FCSTD DOCUMENT  (FreeCAD 0.19R24276 (Git))
Label: Temp_place_bear
License: All rights reserved
LicenseURL: http://en.wikipedia.org/wiki/All_rights_reserved
objects: Sketcher::SketchObject×1, PartDesign::Body×1
note: 2 computed .brp shape members not serialized (recipe doc carries the construction recipe); baked Part::Feature solids carry a one-line shape summary decoded from their .brp

FEATURE [Sketcher::SketchObject] Sketch
  FullyConstrained = false
  MapMode = 5
  Support = -> [XY_Plane]
  sketch-geometry (24):
    g0: LineSegment StartX=0 StartY=0 StartZ=0 EndX=34.4274 EndY=0 EndZ=0
    g1: LineSegment StartX=34.4274 StartY=0 StartZ=0 EndX=34.4274 EndY=10 EndZ=0
    g2: LineSegment StartX=34.4274 StartY=10 StartZ=0 EndX=0 EndY=10 EndZ=0
    g3: LineSegment StartX=0 StartY=10 StartZ=0 EndX=0 EndY=0 EndZ=0
    g4: LineSegment StartX=-18.6453 StartY=16 StartZ=0 EndX=-0.90782 EndY=16 EndZ=0
    g5: LineSegment StartX=-0.90782 StartY=16 StartZ=0 EndX=-0.90782 EndY=5 EndZ=0
    g6: LineSegment StartX=-0.90782 StartY=5 StartZ=0 EndX=-18.6453 EndY=5 EndZ=0
    g7: LineSegment StartX=-18.6453 StartY=5 StartZ=0 EndX=-18.6453 EndY=16 EndZ=0
    g8: LineSegment StartX=3.28213 StartY=20 StartZ=0 EndX=32.8911 EndY=20 EndZ=0
    g9: LineSegment StartX=32.8911 StartY=20 StartZ=0 EndX=32.8911 EndY=10 EndZ=0
    g10: LineSegment StartX=32.8911 StartY=10 StartZ=0 EndX=3.28213 EndY=10 EndZ=0
    g11: LineSegment StartX=3.28213 StartY=10 StartZ=0 EndX=3.28213 EndY=20 EndZ=0
    g12: LineSegment StartX=4.53911 StartY=30 StartZ=0 EndX=22.4162 EndY=30 EndZ=0
    g13: LineSegment StartX=22.4162 StartY=30 StartZ=0 EndX=22.4162 EndY=20 EndZ=0
    g14: LineSegment StartX=22.4162 StartY=20 StartZ=0 EndX=4.53911 EndY=20 EndZ=0
    g15: LineSegment StartX=4.53911 StartY=20 StartZ=0 EndX=4.53911 EndY=30 EndZ=0
    g16: LineSegment StartX=-25.7682 StartY=46 StartZ=0 EndX=-15.1536 EndY=46 EndZ=0
    g17: LineSegment StartX=-15.1536 StartY=46 StartZ=0 EndX=-15.1536 EndY=35 EndZ=0
    g18: LineSegment StartX=-15.1536 StartY=35 StartZ=0 EndX=-25.7682 EndY=35 EndZ=0
    g19: LineSegment StartX=-25.7682 StartY=35 StartZ=0 EndX=-25.7682 EndY=46 EndZ=0
    g20: LineSegment StartX=4.53911 StartY=30 StartZ=0 EndX=18.2263 EndY=30 EndZ=0
    g21: LineSegment StartX=18.2263 StartY=30 StartZ=0 EndX=18.2263 EndY=41 EndZ=0
    g22: LineSegment StartX=18.2263 StartY=41 StartZ=0 EndX=4.53911 EndY=41 EndZ=0
    g23: LineSegment StartX=4.53911 StartY=41 StartZ=0 EndX=4.53911 EndY=30 EndZ=0
  constraints (60):
    c: Coincident(g0,g1)
    c: Coincident(g1,g2)
    c: Coincident(g2,g3)
    c: Coincident(g3,g0)
    c: Horizontal(g0)
    c: Horizontal(g2)
    c: Vertical(g1)
    c: Vertical(g3)
    c: Coincident(g0,g-1)
    c: DistanceY(g1,g1) = 10
    c: Coincident(g4,g5)
    c: Coincident(g5,g6)
    c: Coincident(g6,g7)
    c: Coincident(g7,g4)
    c: Horizontal(g4)
    c: Horizontal(g6)
    c: Vertical(g5)
    c: Vertical(g7)
    c: DistanceY(g7,g7) = 11
    c: DistanceY(g0,g5) = 5
    c: Coincident(g8,g9)
    c: Coincident(g9,g10)
    c: Coincident(g10,g11)
    c: Coincident(g11,g8)
    c: Horizontal(g8)
    c: Horizontal(g10)
    c: Vertical(g9)
    c: Vertical(g11)
    c: DistanceY(g9,g9) = 10
    c: DistanceY(g0,g9) = 10
    c: Coincident(g12,g13)
    c: Coincident(g13,g14)
    c: Coincident(g14,g15)
    c: Coincident(g15,g12)
    c: Horizontal(g12)
    c: Horizontal(g14)
    c: Vertical(g13)
    c: Vertical(g15)
    c: DistanceY(g13,g13) = 10
    c: DistanceY(g0,g13) = 20
    c: Coincident(g16,g17)
    c: Coincident(g17,g18)
    c: Coincident(g18,g19)
    c: Coincident(g19,g16)
    c: Horizontal(g16)
    c: Horizontal(g18)
    c: Vertical(g17)
    c: Vertical(g19)
    c: DistanceY(g19,g19) = 11
    c: DistanceY(g4,g18) = 19
    c: Coincident(g20,g21)
    c: Coincident(g21,g22)
    c: Coincident(g22,g23)
    c: Coincident(g23,g20)
    c: Horizontal(g20)
    c: Horizontal(g22)
    c: Vertical(g21)
    c: Vertical(g23)
    c: Coincident(g20,g12)
    c: DistanceY(g23,g23) = 11
FEATURE [PartDesign::Body] Body
  Group = -> [Sketch]
  Origin = -> Origin
